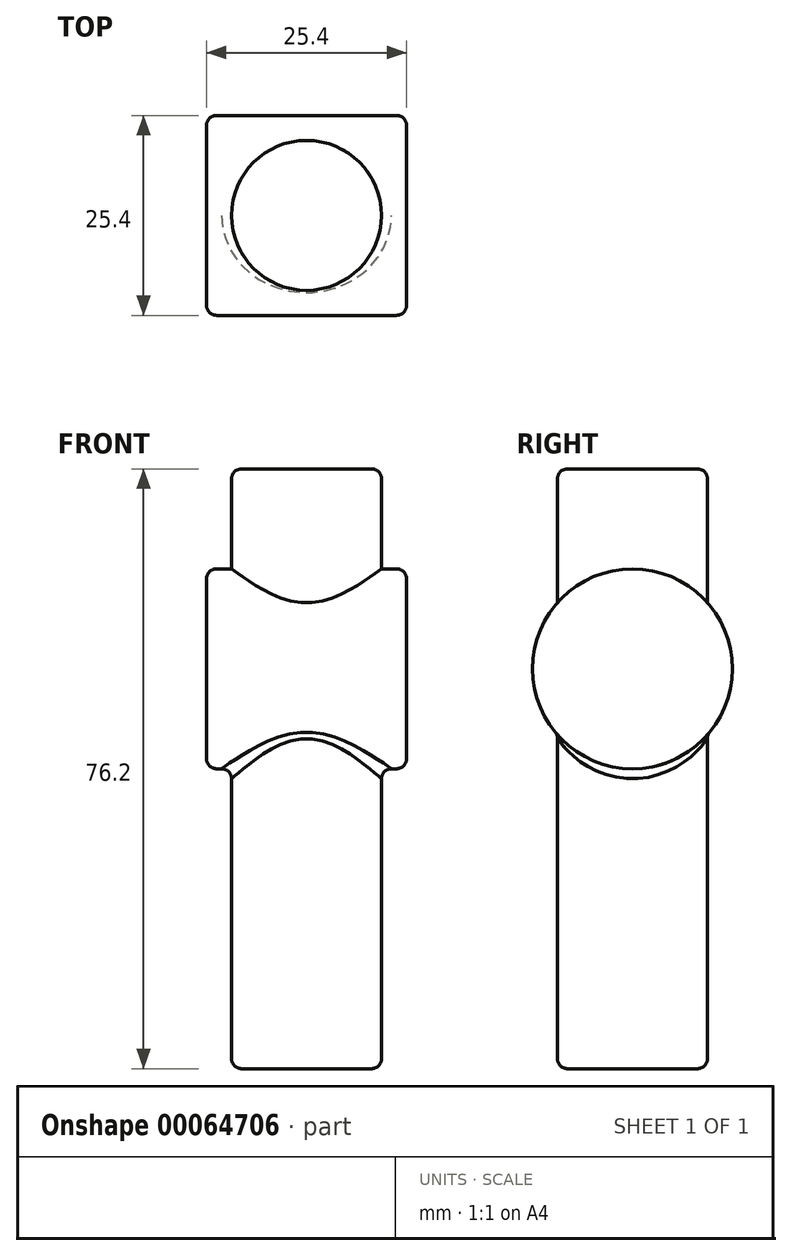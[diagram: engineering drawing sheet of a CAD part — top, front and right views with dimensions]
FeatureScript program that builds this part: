
annotation { "Feature Type Name" : "Feature", "Feature Type Description" : "" }
export const myFeature = defineFeature(function(context is Context, id is Id, definition is map)
    precondition{}
    {
        {
            var Q0;
            Q0=qCreatedBy(makeId("Right.planeOp"),FACE);
            var sketch = newSketch(context, id + "F0", { "sketchPlane" : qUnion([Q0])});
            skCircle(sketch, "E0", {"center": v(0, 0) * mm, "radius": 12.7 * mm});
            skSolve(sketch);
        }
        {
            var Q0;
            Q0 = qSketchRegion(id + "F0", true);
            extrude(context, id + "F1", {"entities" : qUnion([Q0]), "endBound" : BoundingType.SYMMETRIC, "depth" : 25.4 * mm});
        }
        {
            var Q0;
            Q0=qCreatedBy(makeId("Top.planeOp"),FACE);
            var sketch = newSketch(context, id + "F2", { "sketchPlane" : qUnion([Q0])});
            skCircle(sketch, "E1", {"center": v(0, 0) * mm, "radius": 9.53 * mm});
            skSolve(sketch);
        }
        {
            var Q0;
            Q0 = qSketchRegion(id + "F2", true);
            extrude(context, id + "F3", {"entities" : qUnion([Q0]), "operationType" : NewBodyOperationType.ADD, "endBound" : BoundingType.SYMMETRIC, "depth" : 50.8 * mm});
        }
        {
            var Q0;
            Q0=makeQuery(id+"F3.opExtrude","CAP_FACE",FACE,{"disambiguationData":[OSD([sQuery(id+"F2.wireOp",EDGE,"E1")])],"isStart":true});
            var sketch = newSketch(context, id + "F4", { "sketchPlane" : qUnion([Q0])});
            skCircle(sketch, "E2", {"center": v(0, 0) * mm, "radius": 9.53 * mm});
            skSolve(sketch);
        }
        {
            var Q0;
            Q0 = qSketchRegion(id + "F4", true);
            extrude(context, id + "F5", {"entities" : qUnion([Q0]), "operationType" : NewBodyOperationType.ADD, "depth" : 25.4 * mm});
        }
        {
            var Q0;
            Q0=makeQuery(id+"F1.opExtrude","CAP_EDGE",EDGE,{"disambiguationData":[OSD([sQuery(id+"F0.wireOp",EDGE,"E0")])],"isStart":false});
            var Q1;
            Q1=makeQuery(id+"F1.opExtrude","CAP_EDGE",EDGE,{"disambiguationData":[OSD([sQuery(id+"F0.wireOp",EDGE,"E0")])],"isStart":true});
            var Q2;
            Q2=makeQuery(id+"F3.opExtrude","CAP_EDGE",EDGE,{"disambiguationData":[OSD([sQuery(id+"F2.wireOp",EDGE,"E1")])],"isStart":false});
            var Q3;
            {var subQ0=sQuery(id+"F2.wireOp",EDGE,"E1");Q3=makeQuery(id+"F5.boolean.opBoolean","MERGE",FACE,{"derivedFrom":[makeQuery(id+"F3.boolean.opBoolean","SPLIT",FACE,{"disambiguationData":[TD([makeQuery(id+"F3.opExtrude","CAP_FACE",FACE,{"disambiguationData":[OSD([subQ0])],"isStart":true})])],"derivedFrom":makeQuery(id+"F3.opExtrude","SWEPT_FACE",FACE,{"disambiguationData":[OSD([subQ0])]})}),makeQuery(id+"F5.opExtrude","SWEPT_FACE",FACE,{"disambiguationData":[OSD([sQuery(id+"F4.wireOp",EDGE,"E2")])]})]});}
            fillet(context, id + "F6", {"entities" : qUnion([Q0, Q1, Q2, Q3]), "radius" : 1.27 * mm, "tangentPropagation" : true, "allowEdgeOverflow" : false});
        }
    });
